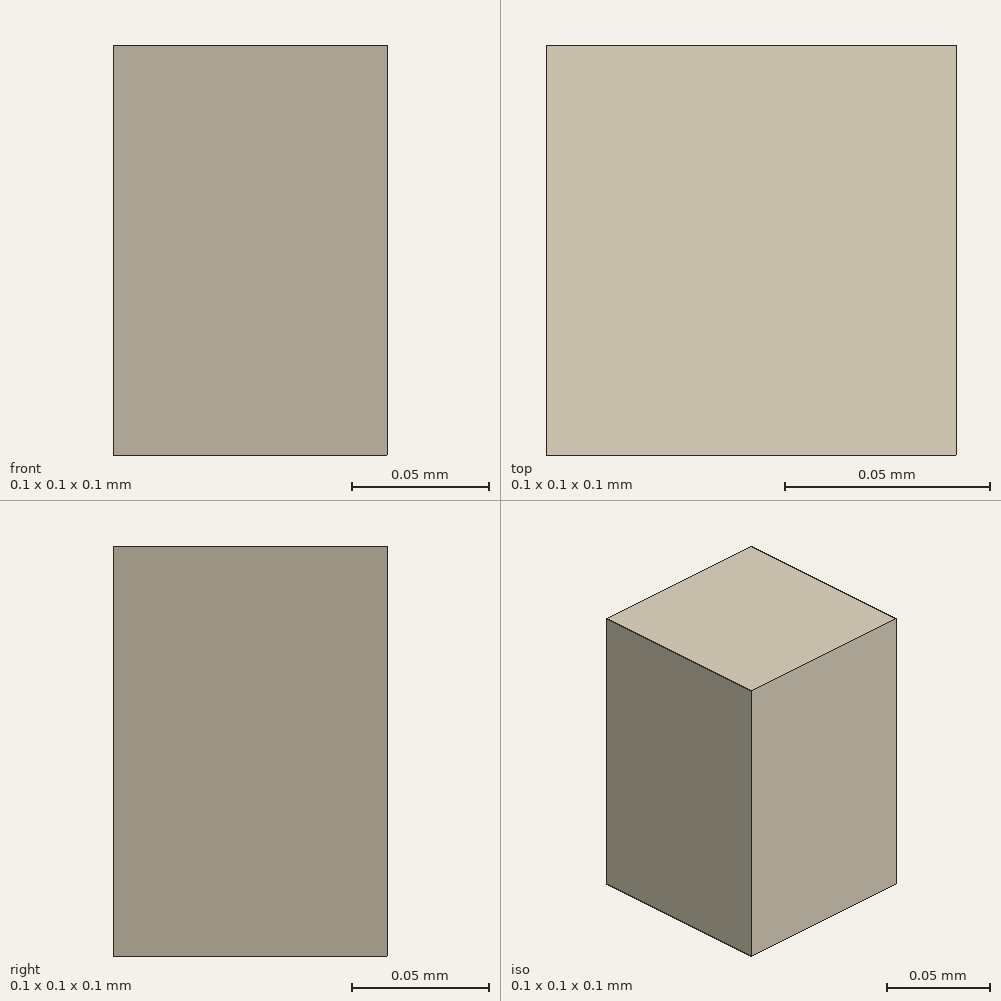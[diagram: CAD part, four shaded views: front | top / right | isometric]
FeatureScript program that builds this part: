
annotation { "Feature Type Name" : "Feature", "Feature Type Description" : "" }
export const myFeature = defineFeature(function(context is Context, id is Id, definition is map)
    precondition{}
    {
        {
            var Q0;
            Q0=qCreatedBy(makeId("Top.planeOp"),FACE);
            var sketch = newSketch(context, id + "F0", { "sketchPlane" : qUnion([Q0])});
            skLineSegment(sketch, "E0.bottom", {"start": v(0, 0) * mm, "end": v(0.1, 0) * mm});
            skLineSegment(sketch, "E0.top", {"start": v(0, -0.1) * mm, "end": v(0.1, -0.1) * mm});
            skLineSegment(sketch, "E0.left", {"start": v(0, 0) * mm, "end": v(0, -0.1) * mm});
            skLineSegment(sketch, "E0.right", {"start": v(0.1, 0) * mm, "end": v(0.1, -0.1) * mm});
            skSolve(sketch);
        }
        {
            var Q0;
            Q0=makeQuery(id+"F0.imprint","IMPRINT",FACE,{"disambiguationData":[TD([[makeQuery(id+"F0.imprint","IMPRINT",EDGE,{"derivedFrom":sQuery(id+"F0.wireOp",EDGE,"E0.bottom")}),-1.0]])]});
            extrude(context, id + "F1", {"entities" : qUnion([Q0]), "depth" : .15 * mm, "offsetDistance" : 25 * mm});
        }
    });
